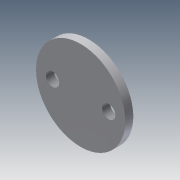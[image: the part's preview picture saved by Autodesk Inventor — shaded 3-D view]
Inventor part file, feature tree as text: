
AUTODESK INVENTOR PART (.ipt)
format: ipt  version: 2015 (Build 190159000, 159)  size: 105,472 bytes
history: native  units: mm
features: sketch x5, extrude x4
ambient origin geometry x8: Origin, YZ Plane, XZ Plane, XY Plane, X Axis, Y Axis, Z Axis, Center Point
bodies: Solid1 (feature_tree)
feature tree (9):
  sketch  "Sketch1"  dims[d0=20.0mm d1=1.8mm d2=0.0mm]
  sketch  "Sketch2"  dims[d3=7.0mm d4=5.0mm]
  extrude  "Extrusion1"  Depth=1.8mm TaperAngle=0.0deg
  extrude  "Extrusion2"  Depth=5.0mm
  extrude  "Extrusion3"  Depth=6.3mm
  extrude  "Extrusion4"  Depth=2.4mm TaperAngle=0.0deg
  sketch  "Sketch3"  dims[d5=2.4mm d6=0.0mm d7=6.3mm]
  sketch  "Sketch4"  dims[d8=3.0mm d9=2.4mm d10=0.0mm]
  sketch  "Sketch5"  dims[d11=6.3mm d12=3.0mm d13=2.0mm d14=0.0mm]
